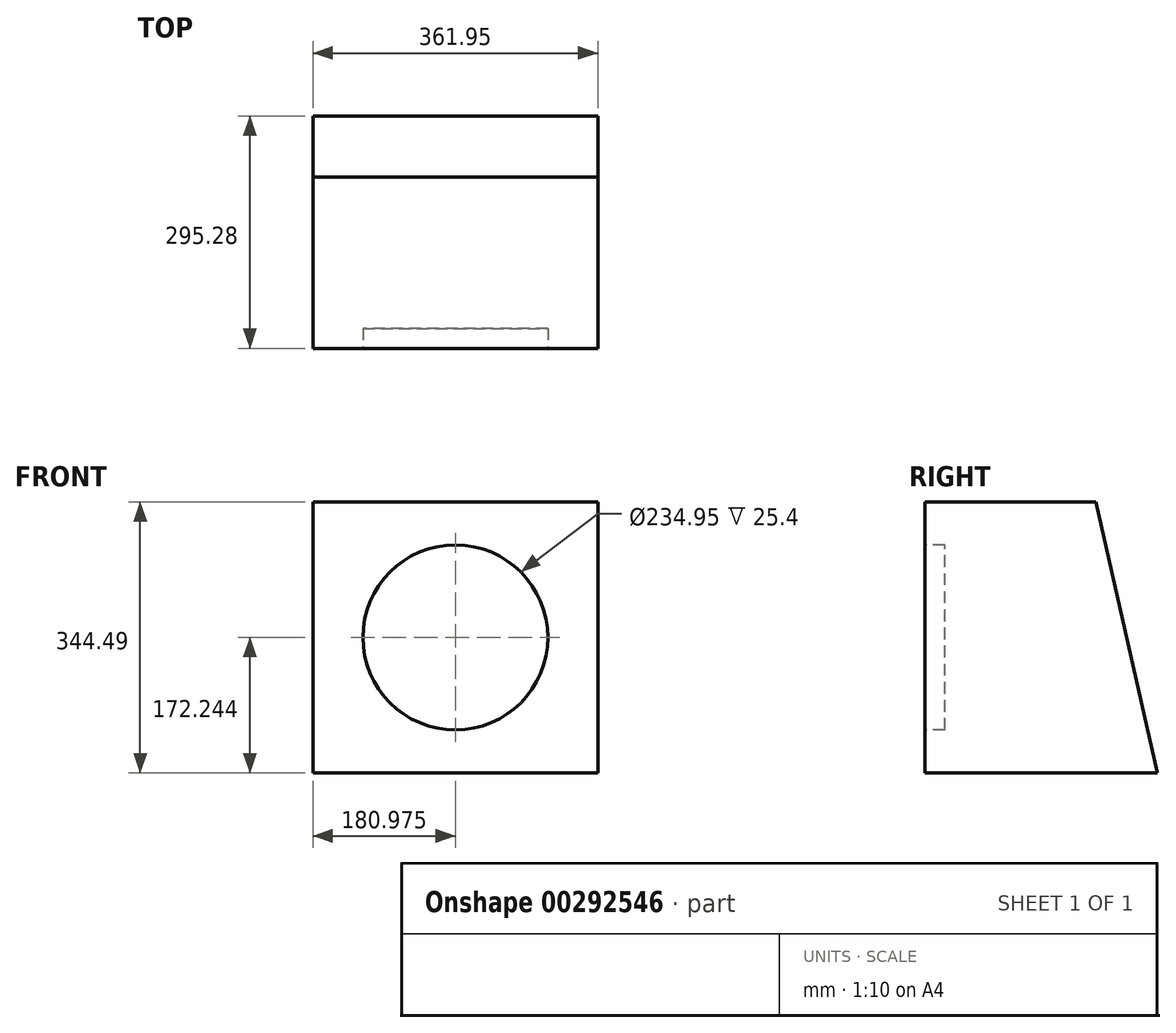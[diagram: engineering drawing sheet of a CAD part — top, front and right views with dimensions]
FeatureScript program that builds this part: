
annotation { "Feature Type Name" : "Feature", "Feature Type Description" : "" }
export const myFeature = defineFeature(function(context is Context, id is Id, definition is map)
    precondition{}
    {
        {
            var Q0;
            Q0=qCreatedBy(makeId("Right.planeOp"),FACE);
            var sketch = newSketch(context, id + "F0", { "sketchPlane" : qUnion([Q0])});
            skLineSegment(sketch, "E0", {"start": v(0, 0) * mm, "end": v(295.27, 0) * mm});
            skLineSegment(sketch, "E1", {"start": v(295.28, 0) * mm, "end": v(217.49, 344.49) * mm});
            skLineSegment(sketch, "E2", {"start": v(217.49, 344.49) * mm, "end": v(0, 344.49) * mm});
            skLineSegment(sketch, "E3", {"start": v(0, 344.49) * mm, "end": v(0, 0) * mm});
            skSolve(sketch);
        }
        {
            var Q0;
            Q0 = qSketchRegion(id + "F0", true);
            extrude(context, id + "F1", {"entities" : qUnion([Q0]), "depth" : 361.95 * mm});
        }
        {
            var Q0;
            Q0=makeQuery(id+"F1.opExtrude","SWEPT_FACE",FACE,{"disambiguationData":[OSD([sQuery(id+"F0.wireOp",EDGE,"E3")])]});
            var sketch = newSketch(context, id + "F2", { "sketchPlane" : qUnion([Q0])});
            skCircle(sketch, "E4", {"center": v(180.98, 172.24) * mm, "radius": 117.48 * mm});
            skLineSegment(sketch, "E5", {"start": v(180.98, 344.49) * mm, "end": v(180.98, 0) * mm, "construction": true});
            skSolve(sketch);
        }
        {
            var Q0;
            Q0 = qSketchRegion(id + "F2", true);
            extrude(context, id + "F3", {"entities" : qUnion([Q0]), "operationType" : NewBodyOperationType.REMOVE, "oppositeDirection" : true, "depth" : 25.4 * mm});
        }
    });
